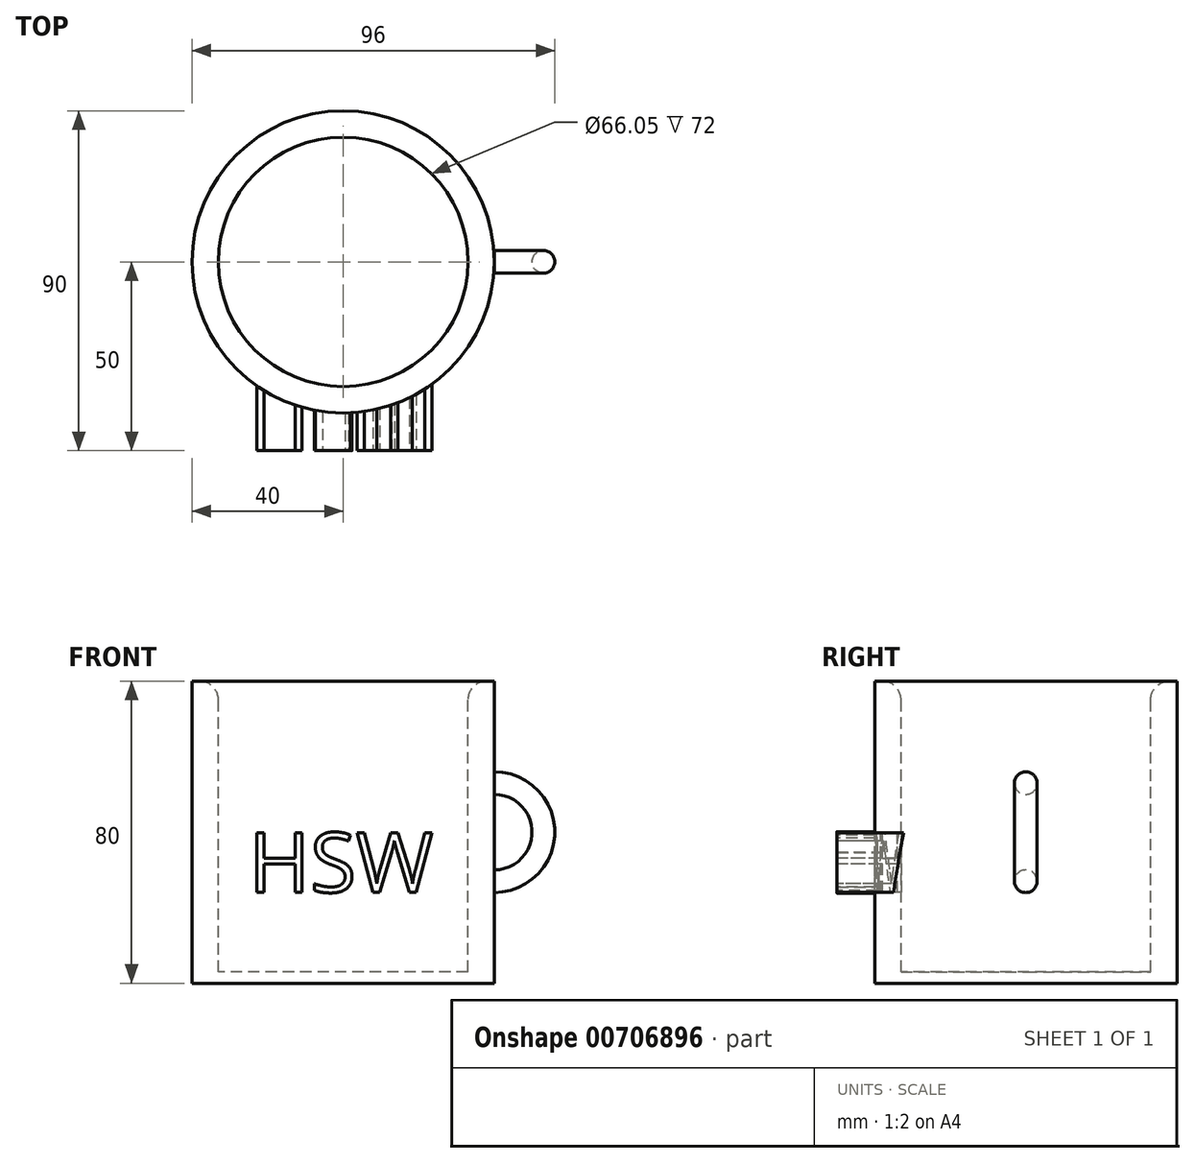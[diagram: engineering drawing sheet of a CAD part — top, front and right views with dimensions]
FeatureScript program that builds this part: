
annotation { "Feature Type Name" : "Feature", "Feature Type Description" : "" }
export const myFeature = defineFeature(function(context is Context, id is Id, definition is map)
    precondition{}
    {
        {
            var Q0;
            Q0=qCreatedBy(makeId("Front.planeOp"),FACE);
            var sketch = newSketch(context, id + "F0", { "sketchPlane" : qUnion([Q0])});
            skLineSegment(sketch, "E0.bottom", {"start": v(38.02, 40) * mm, "end": v(40, 40) * mm});
            skLineSegment(sketch, "E0.top", {"start": v(0, -40) * mm, "end": v(40, -40) * mm});
            skLineSegment(sketch, "E0.left", {"start": v(0, 40) * mm, "end": v(0, -40) * mm});
            skLineSegment(sketch, "E0.right", {"start": v(40, 40) * mm, "end": v(40, -40) * mm});
            skLineSegment(sketch, "E1.top", {"start": v(33.02, -37) * mm, "end": v(0, -37) * mm});
            skLineSegment(sketch, "E1.left", {"start": v(33.02, 35) * mm, "end": v(33.02, -37) * mm});
            skLineSegment(sketch, "E1.right", {"start": v(0, 40) * mm, "end": v(0, -37) * mm});
            skPoint(sketch, "E2.visualSharp", {"position": v(33.02, 40) * mm});
            skArc(sketch, "E2.filletArc", {"start": v(38.02, 40) * mm, "mid": v(34.49, 38.54) * mm, "end": v(33.02, 35) * mm});
            skSolve(sketch);
        }
        {
            var Q0;
            Q0=makeQuery(id+"F0.imprint","IMPRINT",FACE,{"disambiguationData":[TD([[makeQuery(id+"F0.imprint","IMPRINT",EDGE,{"derivedFrom":sQuery(id+"F0.wireOp",EDGE,"E0.bottom")}),-1.0]])]});
            var Q1;
            Q1=sQuery(id+"F0.wireOp",EDGE,"E0.left");
            revolve(context, id + "F1", {"surfaceOperationType" : NewSurfaceOperationType.NEW, "entities" : qUnion([Q0]), "axis" : qUnion([Q1]), "revolveType" : RevolveType.FULL});
        }
        {
            var Q0;
            Q0=qCreatedBy(makeId("Top.planeOp"),FACE);
            var sketch = newSketch(context, id + "F2", { "sketchPlane" : qUnion([Q0])});
            skCircle(sketch, "E3", {"center": v(53, 0) * mm, "radius": 3 * mm});
            skLineSegment(sketch, "E4", {"start": v(40, 26.95) * mm, "end": v(40, -31.84) * mm});
            skSolve(sketch);
        }
        {
            var Q0;
            Q0 = qSketchRegion(id + "F2", true);
            var Q1;
            Q1=sQuery(id+"F2.wireOp",EDGE,"E4");
            revolve(context, id + "F3", {"surfaceOperationType" : NewSurfaceOperationType.NEW, "entities" : qUnion([Q0]), "axis" : qUnion([Q1]), "revolveType" : RevolveType.SYMMETRIC, "oppositeDirection" : true, "angle" : 180 * degree});
        }
        {
            var Q0;
            Q0=qCreatedBy(makeId("Front.planeOp"),FACE);
            cPlane(context, id + "F4", {"entities" : qUnion([Q0]), "cplaneType" : CPlaneType.OFFSET, "offset" : 50 * mm, "width" : 150 * mm, "height" : 150 * mm});
        }
        {
            var Q0;
            Q0=qCreatedBy(id+"F4.planeOp",FACE);
            var sketch = newSketch(context, id + "F5", { "sketchPlane" : qUnion([Q0])});
            skText(sketch, "E5", { "text": "HSW", "fontName": "OpenSans-Regular.ttf"});
            const initialGuessF5  = {"E5": [-0.025, -0.0159, 1, 0, 0.0159]};
            skSetInitialGuess(sketch, initialGuessF5);
            skSolve(sketch);
        }
        {
            var Q0;
            Q0 = qSketchRegion(id + "F5", true);
            extrude(context, id + "F6", {"entities" : qUnion([Q0]), "endBound" : BoundingType.UP_TO_NEXT, "oppositeDirection" : true, "depth" : 25 * mm, "offsetDistance" : 25 * mm});
        }
    });
